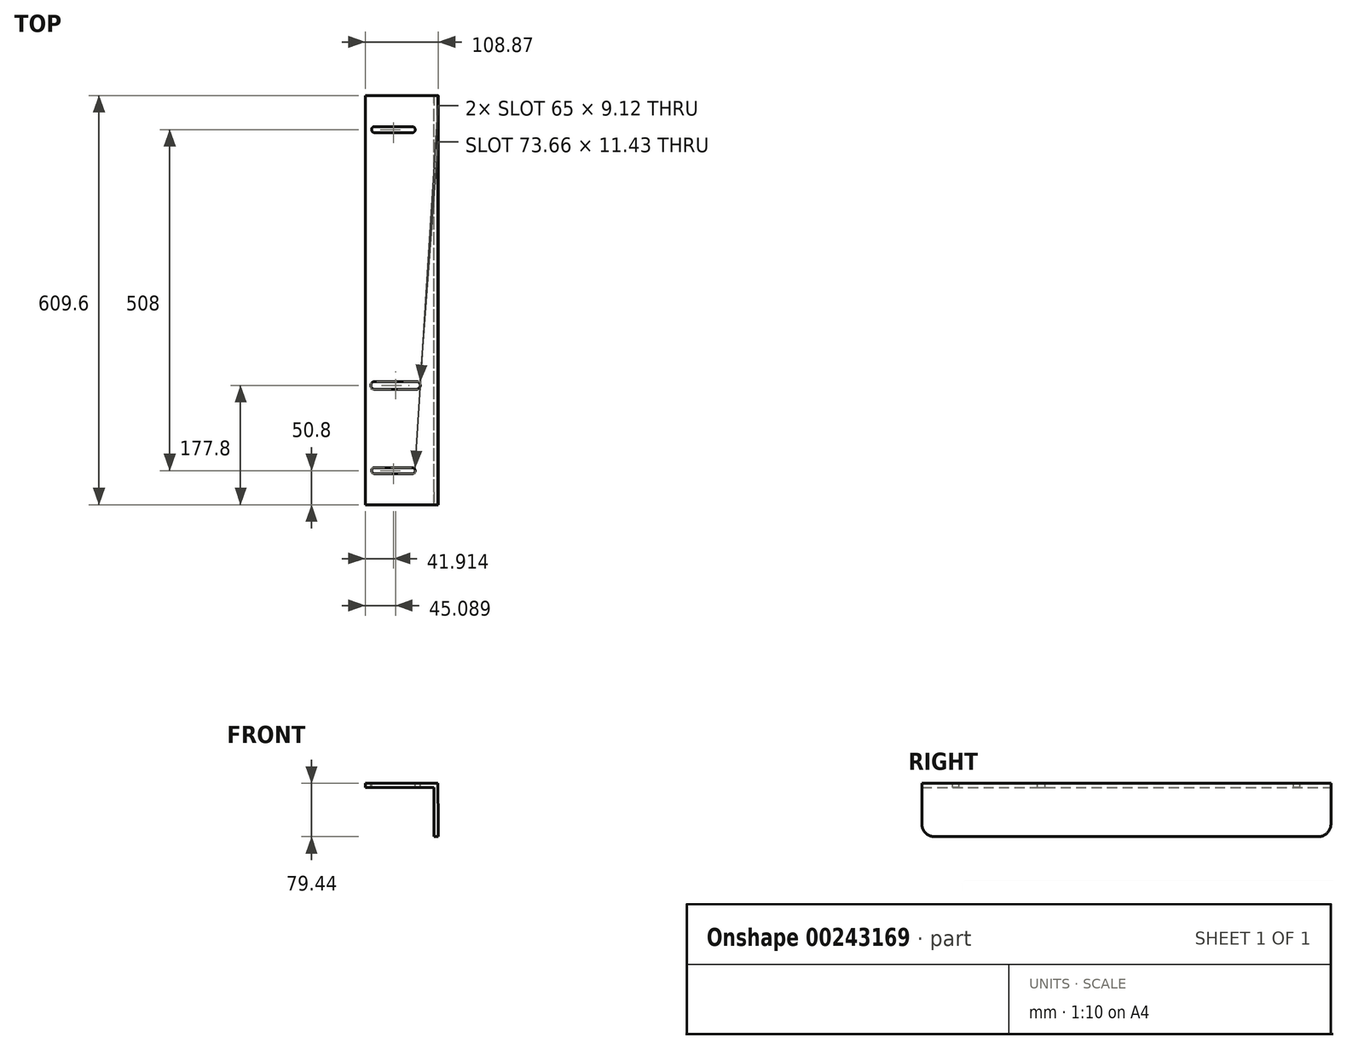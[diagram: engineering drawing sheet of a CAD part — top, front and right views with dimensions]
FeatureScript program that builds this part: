
annotation { "Feature Type Name" : "Feature", "Feature Type Description" : "" }
export const myFeature = defineFeature(function(context is Context, id is Id, definition is map)
    precondition{}
    {
        {
            var Q0;
            Q0=qCreatedBy(makeId("Front.planeOp"),FACE);
            var sketch = newSketch(context, id + "F0", { "sketchPlane" : qUnion([Q0])});
            skLineSegment(sketch, "E0", {"start": v(-102.52, 55.33) * mm, "end": v(-102.52, 48.98) * mm});
            skLineSegment(sketch, "E1", {"start": v(-102.52, 48.98) * mm, "end": v(0, 48.98) * mm});
            skLineSegment(sketch, "E2", {"start": v(-102.52, 55.33) * mm, "end": v(5.43, 55.33) * mm});
            skLineSegment(sketch, "E3", {"start": v(5.43, 55.33) * mm, "end": v(6.35, -24.04) * mm});
            skLineSegment(sketch, "E4", {"start": v(6.35, -24.04) * mm, "end": v(0, -24.1) * mm});
            skLineSegment(sketch, "E5", {"start": v(0, -24.1) * mm, "end": v(0, 48.98) * mm});
            skSolve(sketch);
        }
        {
            var Q0;
            Q0=makeQuery(id+"F0.imprint","IMPRINT",FACE,{"disambiguationData":[TD([[makeQuery(id+"F0.imprint","IMPRINT",EDGE,{"derivedFrom":sQuery(id+"F0.wireOp",EDGE,"E0")}),1.0]])]});
            extrude(context, id + "F1", {"entities" : qUnion([Q0]), "depth" : 609.6 * mm});
        }
        {
            var Q0;
            Q0=makeQuery(id+"F1.opExtrude","SWEPT_FACE",FACE,{"disambiguationData":[OSD([sQuery(id+"F0.wireOp",EDGE,"E2")])]});
            var sketch = newSketch(context, id + "F2", { "sketchPlane" : qUnion([Q0])});
            skLineSegment(sketch, "E6", {"start": v(-48.54, 0) * mm, "end": v(-48.54, -609.6) * mm, "construction": true});
            skArc(sketch, "E7", {"start": v(-88.55, -46.24) * mm, "mid": v(-93.1, -50.8) * mm, "end": v(-88.55, -55.36) * mm});
            skArc(sketch, "E8", {"start": v(-88.55, -554.24) * mm, "mid": v(-93.1, -558.8) * mm, "end": v(-88.55, -563.36) * mm});
            skArc(sketch, "E9", {"start": v(-32.67, -563.36) * mm, "mid": v(-28.1, -558.8) * mm, "end": v(-32.67, -554.24) * mm});
            skLineSegment(sketch, "E10", {"start": v(-88.55, -50.8) * mm, "end": v(-32.67, -50.8) * mm, "construction": true});
            skLineSegment(sketch, "E11", {"start": v(-88.55, -558.8) * mm, "end": v(-32.67, -558.8) * mm, "construction": true});
            skLineSegment(sketch, "E12", {"start": v(-88.55, -46.24) * mm, "end": v(-32.67, -46.24) * mm});
            skLineSegment(sketch, "E13", {"start": v(-88.55, -55.36) * mm, "end": v(-32.67, -55.36) * mm});
            skLineSegment(sketch, "E14", {"start": v(-88.55, -554.24) * mm, "end": v(-32.67, -554.24) * mm});
            skLineSegment(sketch, "E15", {"start": v(-88.55, -563.36) * mm, "end": v(-32.67, -563.36) * mm});
            skArc(sketch, "E16", {"start": v(-32.67, -55.36) * mm, "mid": v(-28.1, -50.8) * mm, "end": v(-32.67, -46.24) * mm});
            skSolve(sketch);
        }
        {
            var Q0;
            Q0=makeQuery(id+"F2.imprint","IMPRINT",FACE,{"disambiguationData":[TD([[makeQuery(id+"F2.imprint","IMPRINT",EDGE,{"derivedFrom":sQuery(id+"F2.wireOp",EDGE,"E7")}),1.0]])]});
            var Q1;
            Q1=makeQuery(id+"F2.imprint","IMPRINT",FACE,{"disambiguationData":[TD([[makeQuery(id+"F2.imprint","IMPRINT",EDGE,{"derivedFrom":sQuery(id+"F2.wireOp",EDGE,"E8")}),1.0]])]});
            extrude(context, id + "F3", {"entities" : qUnion([Q0, Q1]), "operationType" : NewBodyOperationType.REMOVE, "endBound" : BoundingType.THROUGH_ALL, "oppositeDirection" : true, "depth" : 25.4 * mm});
        }
        {
            var Q0;
            Q0=makeQuery(id+"F1.opExtrude","SWEPT_FACE",FACE,{"disambiguationData":[OSD([sQuery(id+"F0.wireOp",EDGE,"E2")])]});
            var sketch = newSketch(context, id + "F4", { "sketchPlane" : qUnion([Q0])});
            skArc(sketch, "E17", {"start": v(-88.55, -426.09) * mm, "mid": v(-94.26, -431.8) * mm, "end": v(-88.55, -437.52) * mm});
            skArc(sketch, "E18", {"start": v(-26.32, -437.52) * mm, "mid": v(-20.6, -431.8) * mm, "end": v(-26.32, -426.09) * mm});
            skLineSegment(sketch, "E19", {"start": v(-26.32, -431.8) * mm, "end": v(-88.55, -431.8) * mm, "construction": true});
            skLineSegment(sketch, "E20", {"start": v(-26.32, -426.09) * mm, "end": v(-88.55, -426.09) * mm});
            skLineSegment(sketch, "E21", {"start": v(-26.32, -437.52) * mm, "end": v(-88.55, -437.52) * mm});
            skSolve(sketch);
        }
        {
            var Q0;
            Q0=makeQuery(id+"F4.imprint","IMPRINT",FACE,{"disambiguationData":[TD([[makeQuery(id+"F4.imprint","IMPRINT",EDGE,{"derivedFrom":sQuery(id+"F4.wireOp",EDGE,"E17")}),1.0]])]});
            extrude(context, id + "F5", {"entities" : qUnion([Q0]), "operationType" : NewBodyOperationType.REMOVE, "endBound" : BoundingType.THROUGH_ALL, "oppositeDirection" : true, "depth" : 25.4 * mm});
        }
        {
            var Q0;
            Q0=makeQuery(id+"F1.opExtrude","CAP_EDGE",EDGE,{"disambiguationData":[OSD([sQuery(id+"F0.wireOp",EDGE,"E4")])],"isStart":false});
            var Q1;
            Q1=makeQuery(id+"F1.opExtrude","CAP_EDGE",EDGE,{"disambiguationData":[OSD([sQuery(id+"F0.wireOp",EDGE,"E4")])],"isStart":true});
            fillet(context, id + "F6", {"entities" : qUnion([Q0, Q1]), "radius" : 19.05 * mm, "tangentPropagation" : true, "allowEdgeOverflow" : false});
        }
    });
